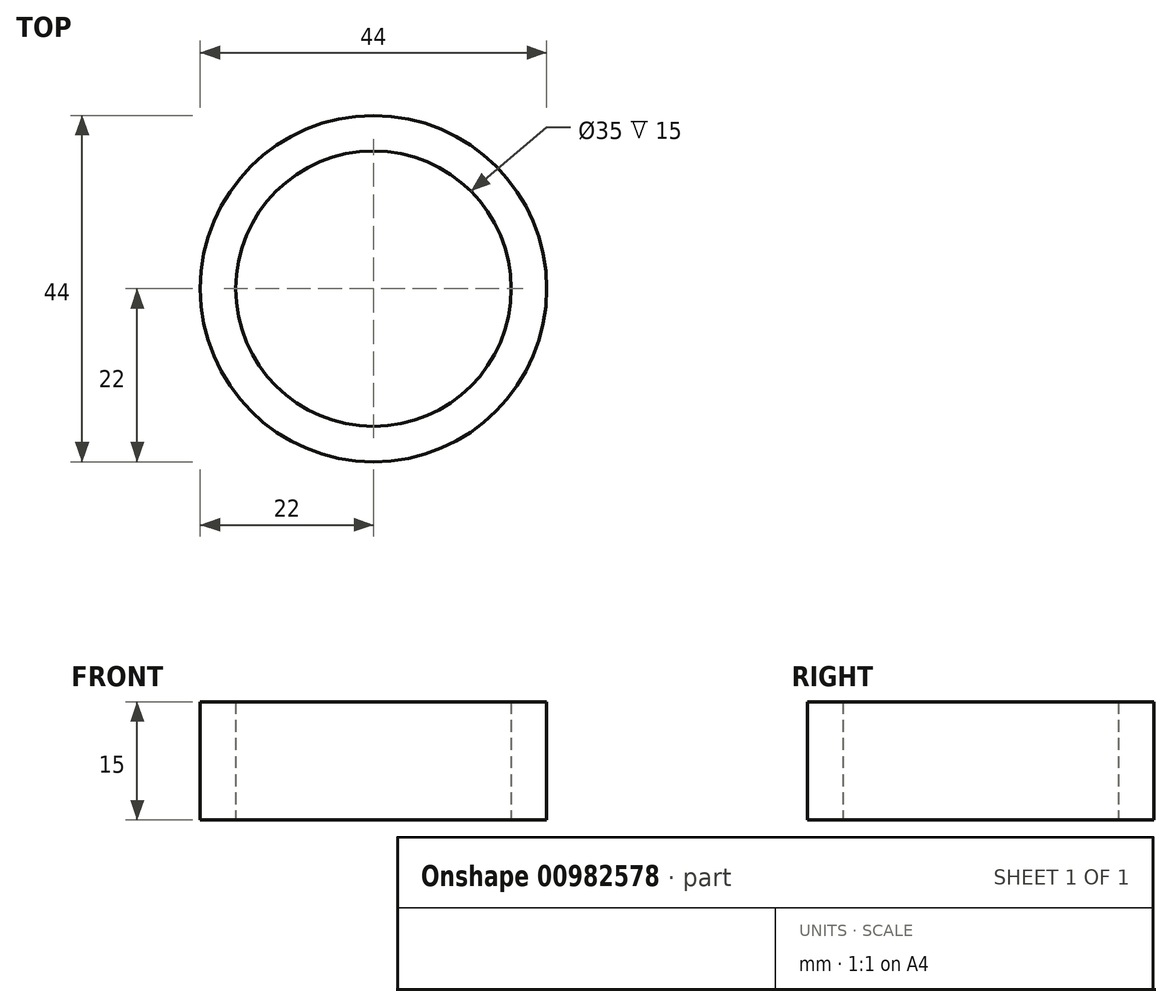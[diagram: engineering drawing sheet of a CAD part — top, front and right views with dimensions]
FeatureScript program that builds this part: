
annotation { "Feature Type Name" : "Feature", "Feature Type Description" : "" }
export const myFeature = defineFeature(function(context is Context, id is Id, definition is map)
    precondition{}
    {
        {
            var Q0;
            Q0=qCreatedBy(makeId("Top.planeOp"),FACE);
            var sketch = newSketch(context, id + "F0", { "sketchPlane" : qUnion([Q0])});
            skCircle(sketch, "E0", {"center": v(0, 0) * mm, "radius": 22 * mm});
            skCircle(sketch, "E1", {"center": v(0, 0) * mm, "radius": 17.5 * mm});
            skSolve(sketch);
        }
        {
            var Q0;
            Q0 = qSketchRegion(id + "F0", true);
            extrude(context, id + "F1", {"entities" : qUnion([Q0]), "depth" : 15 * mm, "offsetDistance" : 25 * mm});
        }
    });
